# Revit family: ACORN LED
name_source: partatom
category: Осветительные приборы
revit_build: Autodesk Revit 2016 (Build: 20161004_0715(x64)
units: mm (PartAtom-declared; Revit-internal decimal feet)

## family parameters
Источник света = Нет
Общий = Нет
Основа = Грань
При загрузке вырезать с полостями = Нет
Размер круглого соединителя = Использовать диаметр
Тип детали = Нормальный
Точка расчета площади = Нет

## types (1)
- ACORN LED
    A = 118 мм
    ADSK_Единица измерения = Шт.
    ADSK_Завод-изготовитель = ООО МГК Световые технологии
    ADSK_Классификация нагрузок = Прочее
    ADSK_Код изделия = 1490000010
    ADSK_Количество фаз = 1
    ADSK_Количество фаз числовое = 1
    ADSK_Коэффициент мощности = 0.96
    ADSK_Масса = 0.6
    ADSK_Наименование = Серия экономичных светильников для замены приборов с лампами накаливания до 500 Вт. Благодаря креплению с помощью скобы, корпусу из качественного сплава, степени защиты IP65, светильник можно установить в производственных помещениях, подвалах, паркингах и многих других похожих площадках. Модификации со стеклянной линзой позволяют использовать светильники ACORN LED в пожароопасных зонах
    ADSK_Напряжение = 230 В
    ADSK_Номинальная мощность = 0 кВт
    ADSK_Полная мощность = 0 кВ·А
    ADSK_Размер_Высота = 169 мм
    ADSK_Размер_Ширина = 140 мм
    ADSK_Ток = 0 А
    ADSK_Энергоэффективность = 98 лм/Вт
    IP Class = IP65
    URL = https://ltcompany.com
    Блок аварийного питания = Нет
    Выбор ИС = IES ACORN LED : ACORN LED 20 D120 5000K
    Группа модели = Светильники
    Да = Нет
    Изготовитель = ООО МГК Световые технологии
    Класс Защиты = I
    Класс пожароопасности = П-II,IIа
    Климатическая зона = УХЛ2
    Код по классификатору = D5020200
    Корпус = Черный металл
    Линза = Плафон прозрачный
    ЛинзаВидимость = Нет
    ЛираВысота = 150 мм
    Нет = Нет
    Область использования = Автостоянки/парковки, ЖКХ, Промышленные предприятия, Складские объекты, Транспортные узлы (вокзалы, аэропорты)
    Описание = Серия экономичных светильников для замены приборов с лампами накаливания до 500 Вт. Благодаря креплению с помощью скобы, корпусу из качественного сплава, степени защиты IP65, светильник можно установить в производственных помещениях, подвалах, паркингах и многих других похожих площадках. Модификации со стеклянной линзой позволяют использовать светильники ACORN LED в пожароопасных зонах
    ОсьВращения = 105 мм
    Отметка по умолчанию = 0 мм
    Плафон = Плафон полупрозрачный
    ПлафонВидимость = Да
    Полная установленная мощность = 0 кВ·А
    Рым-болт = Корпус металл
    Тип ИС = LED
    Тип ПРА = Драйвер
    Тип продукции = Светильник

## geometry (parser evidence)
native form markers: Blend x4
no freeform markers — native parametric forms only
